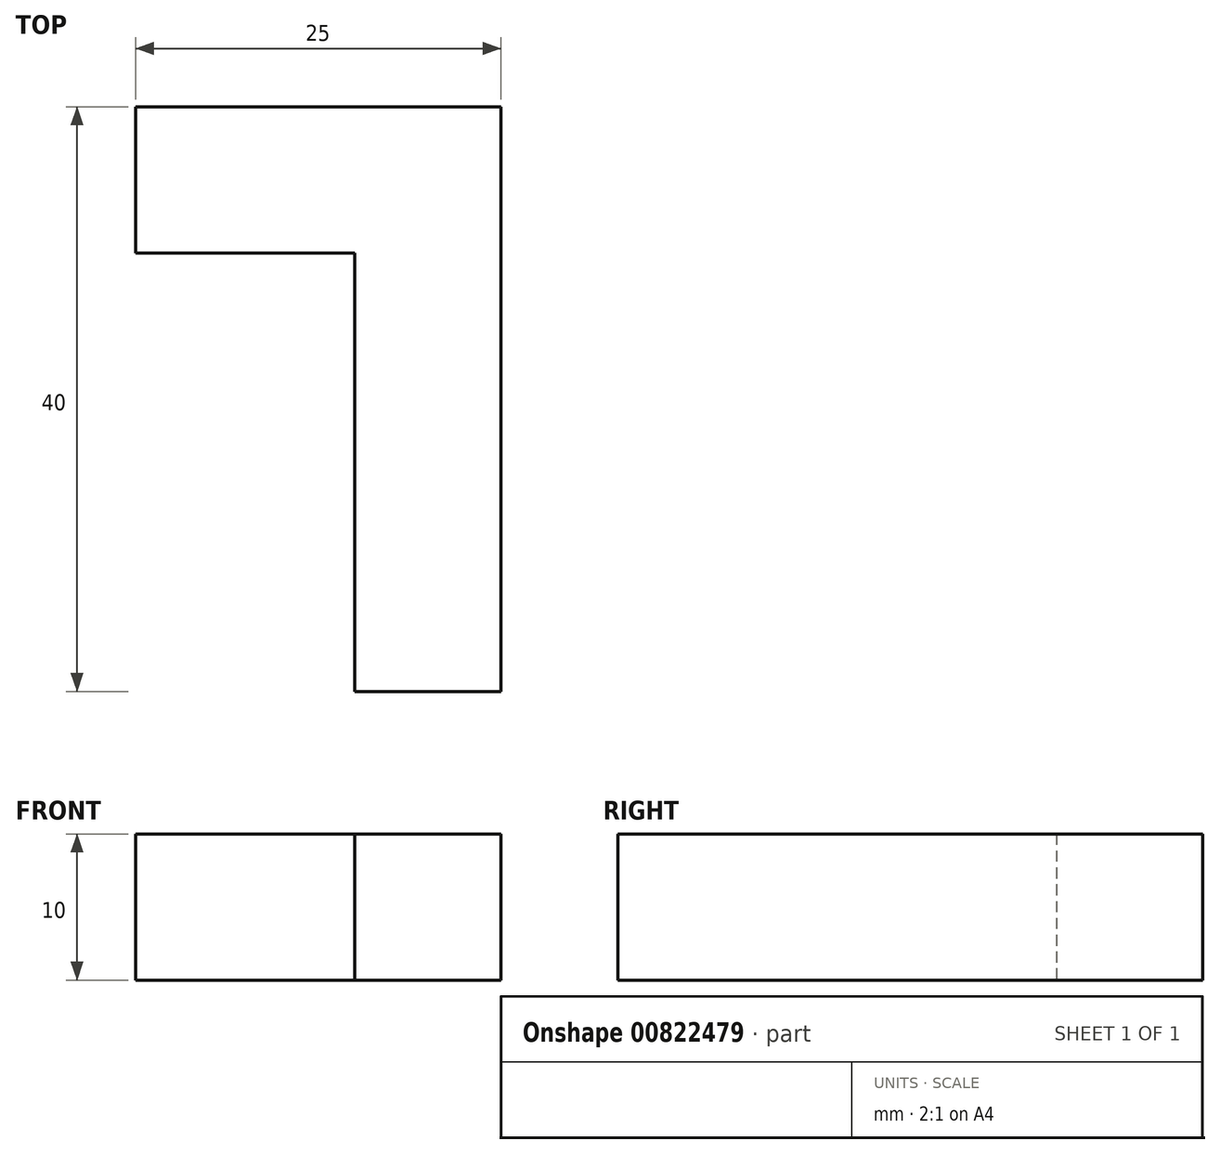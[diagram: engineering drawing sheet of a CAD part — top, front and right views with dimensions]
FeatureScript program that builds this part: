
annotation { "Feature Type Name" : "Feature", "Feature Type Description" : "" }
export const myFeature = defineFeature(function(context is Context, id is Id, definition is map)
    precondition{}
    {
        {
            var Q0;
            Q0=qCreatedBy(makeId("Top.planeOp"),FACE);
            var sketch = newSketch(context, id + "F0", { "sketchPlane" : qUnion([Q0])});
            skLineSegment(sketch, "E0.bottom", {"start": v(-25, 28.4) * mm, "end": v(0, 28.4) * mm});
            skLineSegment(sketch, "E0.left", {"start": v(-25, 28.4) * mm, "end": v(-25, 18.4) * mm});
            skLineSegment(sketch, "E1.top", {"start": v(-10, -11.6) * mm, "end": v(0, -11.6) * mm});
            skLineSegment(sketch, "E1.left", {"start": v(-10, 18.4) * mm, "end": v(-10, -11.6) * mm});
            skLineSegment(sketch, "E2", {"start": v(-25, 18.4) * mm, "end": v(-10, 18.4) * mm});
            skLineSegment(sketch, "E3", {"start": v(0, 28.4) * mm, "end": v(0, -11.6) * mm});
            skSolve(sketch);
        }
        {
            var Q0;
            Q0=makeQuery(id+"F0.imprint","IMPRINT",FACE,{"disambiguationData":[TD([[makeQuery(id+"F0.imprint","IMPRINT",EDGE,{"derivedFrom":sQuery(id+"F0.wireOp",EDGE,"E0.bottom")}),-1.0]])]});
            extrude(context, id + "F1", {"entities" : qUnion([Q0]), "depth" : 10 * mm, "offsetDistance" : 25 * mm});
        }
    });
